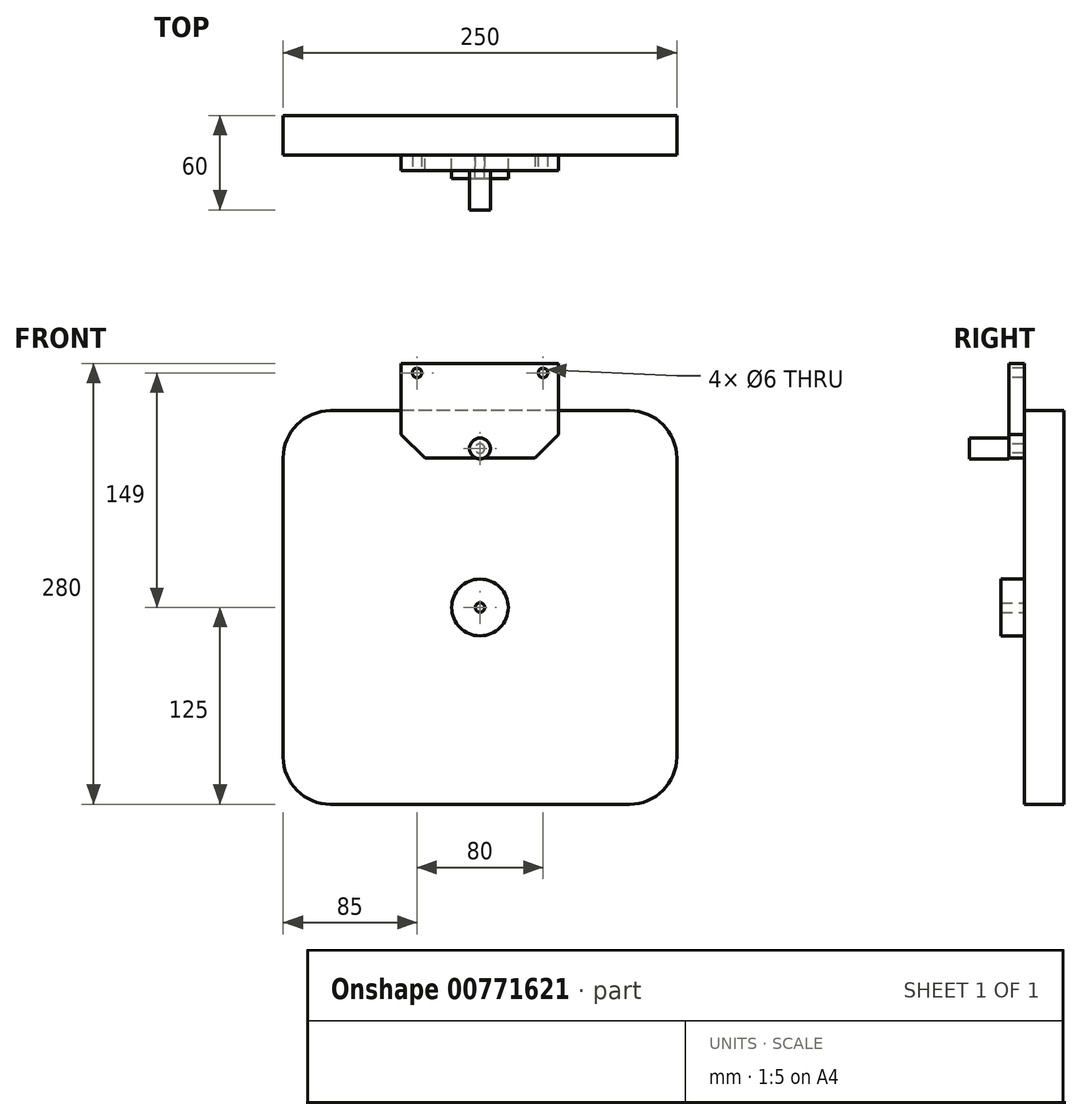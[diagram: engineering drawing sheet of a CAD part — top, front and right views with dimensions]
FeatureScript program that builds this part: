
annotation { "Feature Type Name" : "Feature", "Feature Type Description" : "" }
export const myFeature = defineFeature(function(context is Context, id is Id, definition is map)
    precondition{}
    {
        {
            var Q0;
            Q0=qCreatedBy(makeId("Front.planeOp"),FACE);
            var sketch = newSketch(context, id + "F0", { "sketchPlane" : qUnion([Q0])});
            skLineSegment(sketch, "E0.bottom", {"start": v(95, 125) * mm, "end": v(-95, 125) * mm});
            skLineSegment(sketch, "E0.top", {"start": v(95, -125) * mm, "end": v(-95, -125) * mm});
            skLineSegment(sketch, "E0.left", {"start": v(125, 95) * mm, "end": v(125, -95) * mm});
            skLineSegment(sketch, "E0.right", {"start": v(-125, 95) * mm, "end": v(-125, -95) * mm});
            skPoint(sketch, "E0.middle", {"position": v(0, 0) * mm});
            skPoint(sketch, "E1.visualSharp", {"position": v(-125, 125) * mm});
            skArc(sketch, "E1.filletArc", {"start": v(-95, 125) * mm, "mid": v(-116.21, 116.21) * mm, "end": v(-125, 95) * mm});
            skPoint(sketch, "E2.visualSharp", {"position": v(125, 125) * mm});
            skArc(sketch, "E2.filletArc", {"start": v(125, 95) * mm, "mid": v(116.21, 116.21) * mm, "end": v(95, 125) * mm});
            skPoint(sketch, "E3.visualSharp", {"position": v(125, -125) * mm});
            skArc(sketch, "E3.filletArc", {"start": v(95, -125) * mm, "mid": v(116.21, -116.21) * mm, "end": v(125, -95) * mm});
            skPoint(sketch, "E4.visualSharp", {"position": v(-125, -125) * mm});
            skArc(sketch, "E4.filletArc", {"start": v(-125, -95) * mm, "mid": v(-116.21, -116.21) * mm, "end": v(-95, -125) * mm});
            skSolve(sketch);
        }
        {
            var Q0;
            Q0=makeQuery(id+"F0.imprint","IMPRINT",FACE,{"disambiguationData":[TD([[makeQuery(id+"F0.imprint","IMPRINT",EDGE,{"derivedFrom":sQuery(id+"F0.wireOp",EDGE,"E0.bottom")}),1.0]])]});
            extrude(context, id + "F1", {"entities" : qUnion([Q0]), "oppositeDirection" : true, "depth" : 25 * mm, "offsetDistance" : 25 * mm});
        }
        {
            var Q0;
            Q0=makeQuery(id+"F1.opExtrude","CAP_FACE",FACE,{"disambiguationData":[OSD([sQuery(id+"F0.wireOp",EDGE,"E0.bottom"),sQuery(id+"F0.wireOp",EDGE,"E0.top"),sQuery(id+"F0.wireOp",EDGE,"E0.left"),sQuery(id+"F0.wireOp",EDGE,"E0.right"),sQuery(id+"F0.wireOp",EDGE,"E1.filletArc"),sQuery(id+"F0.wireOp",EDGE,"E2.filletArc"),sQuery(id+"F0.wireOp",EDGE,"E3.filletArc"),sQuery(id+"F0.wireOp",EDGE,"E4.filletArc")])],"isStart":true});
            var sketch = newSketch(context, id + "F2", { "sketchPlane" : qUnion([Q0])});
            skCircle(sketch, "E5", {"center": v(0, 0) * mm, "radius": 18 * mm});
            skCircle(sketch, "E6", {"center": v(0, 0) * mm, "radius": 3 * mm});
            skSolve(sketch);
        }
        {
            var Q0;
            Q0=makeQuery(id+"F2.imprint","IMPRINT",FACE,{"disambiguationData":[TD([[makeQuery(id+"F2.imprint","IMPRINT",EDGE,{"derivedFrom":sQuery(id+"F2.wireOp",EDGE,"E5")}),1.0]])]});
            extrude(context, id + "F3", {"entities" : qUnion([Q0]), "depth" : 15 * mm, "offsetDistance" : 25 * mm});
        }
        {
            var Q0;
            Q0=makeQuery(id+"F1.opExtrude","CAP_FACE",FACE,{"disambiguationData":[OSD([sQuery(id+"F0.wireOp",EDGE,"E0.bottom"),sQuery(id+"F0.wireOp",EDGE,"E0.top"),sQuery(id+"F0.wireOp",EDGE,"E0.left"),sQuery(id+"F0.wireOp",EDGE,"E0.right"),sQuery(id+"F0.wireOp",EDGE,"E1.filletArc"),sQuery(id+"F0.wireOp",EDGE,"E2.filletArc"),sQuery(id+"F0.wireOp",EDGE,"E3.filletArc"),sQuery(id+"F0.wireOp",EDGE,"E4.filletArc")])],"isStart":true});
            var sketch = newSketch(context, id + "F4", { "sketchPlane" : qUnion([Q0])});
            skLineSegment(sketch, "E7.bottom", {"start": v(50, 95) * mm, "end": v(-50, 95) * mm});
            skLineSegment(sketch, "E7.top", {"start": v(50, 155) * mm, "end": v(-50, 155) * mm});
            skLineSegment(sketch, "E7.left", {"start": v(50, 95) * mm, "end": v(50, 155) * mm});
            skLineSegment(sketch, "E7.right", {"start": v(-50, 95) * mm, "end": v(-50, 155) * mm});
            skPoint(sketch, "E7.middle", {"position": v(0, 125) * mm});
            skSolve(sketch);
        }
        {
            var Q0;
            {var subQ0=sQuery(id+"F4.wireOp",EDGE,"E7.top");Q0=makeQuery(id+"F4.imprint","IMPRINT",FACE,{"disambiguationData":[TD([[makeQuery(id+"F4.imprint","IMPRINT",EDGE,{"derivedFrom":subQ0}),1.0]])]});}
            var Q1;
            {var subQ0=sQuery(id+"F4.wireOp",EDGE,"E7.bottom");Q1=makeQuery(id+"F4.imprint","IMPRINT",FACE,{"disambiguationData":[TD([[makeQuery(id+"F4.imprint","IMPRINT",EDGE,{"derivedFrom":subQ0}),-1.0]])]});}
            extrude(context, id + "F5", {"entities" : qUnion([Q0, Q1]), "depth" : 10 * mm, "offsetDistance" : 25 * mm});
        }
        {
            var Q0;
            Q0=makeQuery(id+"F5.opExtrude","CAP_FACE",FACE,{"disambiguationData":[OSD([sQuery(id+"F4.wireOp",EDGE,"E7.bottom"),sQuery(id+"F4.wireOp",EDGE,"E7.top"),sQuery(id+"F4.wireOp",EDGE,"E7.left"),sQuery(id+"F4.wireOp",EDGE,"E7.right")])],"isStart":false});
            var sketch = newSketch(context, id + "F6", { "sketchPlane" : qUnion([Q0])});
            skLineSegment(sketch, "E8", {"start": v(-40, 149) * mm, "end": v(40, 149) * mm});
            skLineSegment(sketch, "E9", {"start": v(0, 149) * mm, "end": v(0, 101) * mm});
            skLineSegment(sketch, "E10", {"start": v(0, 149) * mm, "end": v(0, 155) * mm});
            skCircle(sketch, "E11", {"center": v(-40, 149) * mm, "radius": 3 * mm});
            skCircle(sketch, "E12", {"center": v(40, 149) * mm, "radius": 3 * mm});
            skCircle(sketch, "E13", {"center": v(0, 101) * mm, "radius": 3 * mm});
            skSolve(sketch);
        }
        {
            var Q0;
            Q0=makeQuery(id+"F6.imprint","IMPRINT",FACE,{"disambiguationData":[TD([[makeQuery(id+"F6.imprint","IMPRINT",EDGE,{"derivedFrom":sQuery(id+"F6.wireOp",EDGE,"E11")}),1.0]])]});
            var Q1;
            Q1=makeQuery(id+"F6.imprint","IMPRINT",FACE,{"disambiguationData":[TD([[makeQuery(id+"F6.imprint","IMPRINT",EDGE,{"derivedFrom":sQuery(id+"F6.wireOp",EDGE,"E13")}),1.0]])]});
            var Q2;
            Q2=makeQuery(id+"F6.imprint","IMPRINT",FACE,{"disambiguationData":[TD([[makeQuery(id+"F6.imprint","IMPRINT",EDGE,{"derivedFrom":sQuery(id+"F6.wireOp",EDGE,"E12")}),1.0]])]});
            extrude(context, id + "F7", {"entities" : qUnion([Q0, Q1, Q2]), "operationType" : NewBodyOperationType.REMOVE, "endBound" : BoundingType.UP_TO_NEXT, "oppositeDirection" : true, "depth" : 25 * mm, "offsetDistance" : 25 * mm});
        }
        {
            var Q0;
            Q0=makeQuery(id+"F5.opExtrude","SWEPT_EDGE",EDGE,{"disambiguationData":[OSD([sQuery(id+"F4.wireOp",EDGE,"E7.bottom"),sQuery(id+"F4.wireOp",EDGE,"E7.left")])]});
            var Q1;
            Q1=makeQuery(id+"F5.opExtrude","SWEPT_EDGE",EDGE,{"disambiguationData":[OSD([sQuery(id+"F4.wireOp",EDGE,"E7.bottom"),sQuery(id+"F4.wireOp",EDGE,"E7.right")])]});
            chamfer(context, id + "F8", {"entities" : qUnion([Q0, Q1]), "width" : 15 * mm, "tangentPropagation" : true});
        }
        {
            var Q0;
            Q0=makeQuery(id+"F5.opExtrude","CAP_FACE",FACE,{"disambiguationData":[OSD([sQuery(id+"F4.wireOp",EDGE,"E7.bottom"),sQuery(id+"F4.wireOp",EDGE,"E7.top"),sQuery(id+"F4.wireOp",EDGE,"E7.left"),sQuery(id+"F4.wireOp",EDGE,"E7.right")])],"isStart":false});
            var sketch = newSketch(context, id + "F9", { "sketchPlane" : qUnion([Q0])});
            skCircle(sketch, "E14", {"center": v(0, 101) * mm, "radius": 6.63 * mm});
            skCircle(sketch, "E15.0", {"center": v(0, 101) * mm, "radius": 3 * mm});
            skSolve(sketch);
        }
        {
            var Q0;
            Q0=makeQuery(id+"F9.imprint","IMPRINT",FACE,{"disambiguationData":[TD([[makeQuery(id+"F9.imprint","IMPRINT",EDGE,{"derivedFrom":sQuery(id+"F9.wireOp",EDGE,"E15.0")}),1.0]])]});
            extrude(context, id + "F10", {"entities" : qUnion([Q0]), "oppositeDirection" : true, "depth" : 10 * mm, "offsetDistance" : 25 * mm});
        }
        {
            var Q0;
            Q0 = qSketchRegion(id + "F9", true);
            var Q1;
            Q1=makeQuery(id+"F10.opExtrude","CAP_FACE",FACE,{"disambiguationData":[OSD([sQuery(id+"F9.wireOp",EDGE,"E15.0")])],"isStart":true});
            extrude(context, id + "F11", {"entities" : qUnion([Q0, Q1]), "depth" : 25 * mm, "offsetDistance" : 25 * mm});
        }
        {
            var Q0;
            Q0=makeQuery(id+"F10.opExtrude","SWEPT_BODY",BODY,{"disambiguationData":[OSD([sQuery(id+"F9.wireOp",EDGE,"E15.0")])]});
            var Q1;
            Q1=makeQuery(id+"F11.opExtrude","SWEPT_BODY",BODY,{"disambiguationData":[OSD([sQuery(id+"F9.wireOp",EDGE,"E14"),sQuery(id+"F9.wireOp",EDGE,"E15.0")])]});
            var Q2;
            Q2=makeQuery(id+"F11.opExtrude","SWEPT_BODY",BODY,{"disambiguationData":[OSD([sQuery(id+"F9.wireOp",EDGE,"E15.0")])]});
            booleanBodies(context, id + "F12", {"operationType" : BooleanOperationType.UNION, "tools" : qUnion([Q0, Q1, Q2])});
        }
    });
